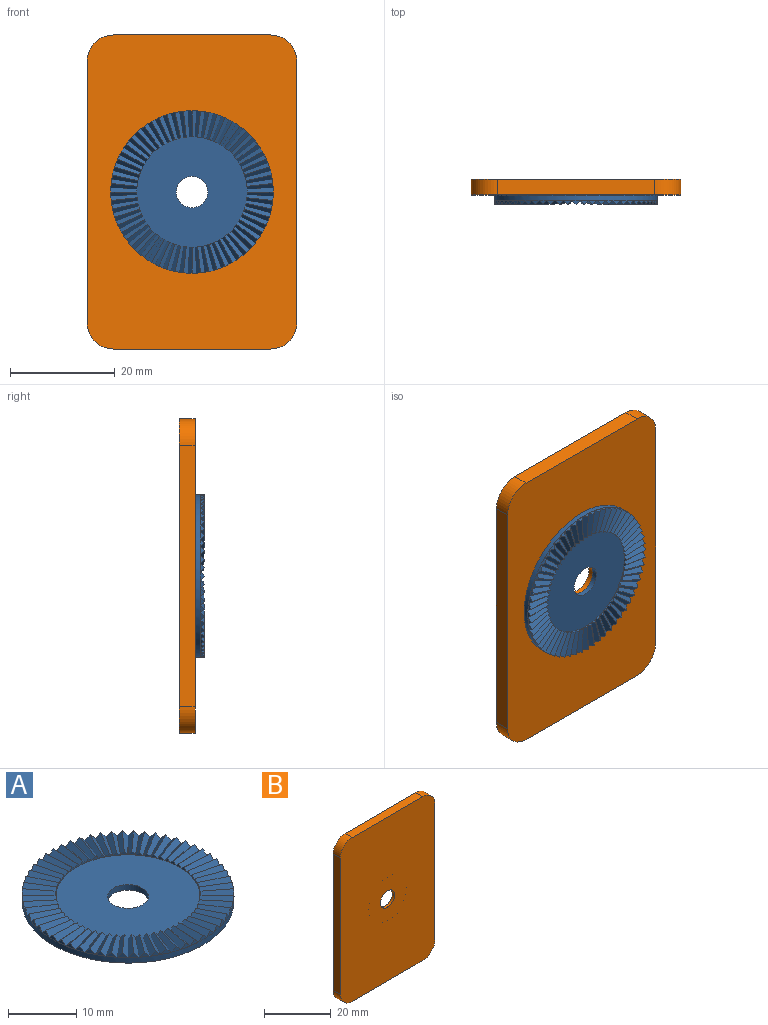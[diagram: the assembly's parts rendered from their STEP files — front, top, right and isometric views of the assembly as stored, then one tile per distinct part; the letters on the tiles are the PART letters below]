
ASSEMBLY  parts=2 mates=1
PART A: 364 faces, bbox 31x31x1.8 mm
  f0: plane 30.96x30.96mm, normal (0,0,1), area 322.4mm2, adj f1,f2,f6,f7,f9,f12,f13,f15
  f1: cylinder r=3mm len=6mm, axis (0,0,1), area 18.8mm2, adj f0,f3
  f2: cylinder r=15.5mm len=31mm, axis (0,0,1), area 97.4mm2, adj f0,f3,f4,f8,f10,f14,f16,f20
  f3: plane 31x31mm, normal (0,0,-1), area 726.5mm2, adj f1,f2
  f4: plane 0.81x0.02mm, normal (0,0,-1), area 0mm2, adj f2,f5,f9
  f5: plane 1.62x0.81mm, normal (-1,0,0), area 0.7mm2, adj f4,f7,f8,f9
  f6: plane 1.1x0.55mm, normal (1,0,0), area 0.3mm2, adj f0,f7,f9
  f7: plane 4.95x0.81mm, normal (0.04,-0.71,0.71), area 4.8mm2, adj f0,f5,f6,f8,f9
  f8: plane 0.81x0.02mm, normal (0,0,-1), area 0mm2, adj f2,f5,f7
  f9: plane 4.95x0.81mm, normal (0.04,0.71,0.71), area 4.8mm2, adj f0,f4,f5,f6,f7
  f10: plane 0.81x0.08mm, normal (0,0,-1), area 0mm2, adj f2,f11,f15
  f11: plane 1.61x0.81mm, normal (-0.99,-0.1,0), area 0.7mm2, adj f10,f13,f14,f15
  f12: plane 1.1x0.55mm, normal (0.99,0.1,0), area 0.3mm2, adj f0,f13,f15
  f13: plane 4.98x1.32mm, normal (0.11,-0.7,0.71), area 4.8mm2, adj f0,f11,f12,f14,f15
  f14: plane 0.81x0.11mm, normal (0,0,-1), area 0mm2, adj f2,f11,f13
  f15: plane 5.01x1.07mm, normal (-0.04,0.71,0.71), area 4.8mm2, adj f0,f10,f11,f12,f13
  f16: plane 0.8x0.17mm, normal (0,0,-1), area 0mm2, adj f2,f17,f21
  f17: plane 1.59x0.81mm, normal (-0.98,-0.21,0), area 0.7mm2, adj f16,f19,f20,f21
  f18: plane 1.08x0.55mm, normal (0.98,0.21,0), area 0.3mm2, adj f0,f19,f21
  f19: plane 4.95x1.82mm, normal (0.18,-0.68,0.71), area 4.8mm2, adj f0,f17,f18,f20,f21
  f20: plane 0.79x0.19mm, normal (0,0,-1), area 0mm2, adj f2,f17,f19
  f21: plane 5.01x1.57mm, normal (-0.11,0.7,0.71), area 4.8mm2, adj f0,f16,f17,f18,f19
  f22: plane 0.78x0.25mm, normal (0,0,-1), area 0mm2, adj f2,f23,f27
  f23: plane 1.54x0.81mm, normal (-0.95,-0.31,0), area 0.7mm2, adj f22,f25,f26,f27
  f24: plane 1.05x0.55mm, normal (0.95,0.31,0), area 0.3mm2, adj f0,f25,f27
  f25: plane 4.88x2.3mm, normal (0.25,-0.66,0.71), area 4.8mm2, adj f0,f23,f24,f26,f27
  f26: plane 0.77x0.27mm, normal (0,0,-1), area 0mm2, adj f2,f23,f25
  f27: plane 4.96x2.05mm, normal (-0.18,0.68,0.71), area 4.8mm2, adj f0,f22,f23,f24,f25
  f28: plane 0.75x0.33mm, normal (0,0,-1), area 0mm2, adj f2,f29,f33
  f29: plane 1.48x0.81mm, normal (-0.91,-0.41,0), area 0.7mm2, adj f28,f31,f32,f33
  f30: plane 1.01x0.55mm, normal (0.91,0.41,0), area 0.3mm2, adj f0,f31,f33
  f31: plane 4.74x2.75mm, normal (0.32,-0.63,0.71), area 4.8mm2, adj f0,f29,f30,f32,f33
  f32: plane 0.74x0.35mm, normal (0,0,-1), area 0mm2, adj f2,f29,f31
  f33: plane 4.85x2.52mm, normal (-0.25,0.66,0.71), area 4.8mm2, adj f0,f28,f29,f30,f31
  f34: plane 0.71x0.41mm, normal (0,0,-1), area 0mm2, adj f2,f35,f39
  f35: plane 1.41x0.81mm, normal (-0.87,-0.5,0), area 0.7mm2, adj f34,f37,f38,f39
  f36: plane 0.96x0.55mm, normal (0.87,0.5,0), area 0.3mm2, adj f0,f37,f39
  f37: plane 4.56x3.18mm, normal (0.39,-0.59,0.71), area 4.8mm2, adj f0,f35,f36,f38,f39
  f38: plane 0.7x0.42mm, normal (0,0,-1), area 0mm2, adj f2,f35,f37
  f39: plane 4.69x2.95mm, normal (-0.32,0.63,0.71), area 4.8mm2, adj f0,f34,f35,f36,f37
  f40: plane 0.67x0.48mm, normal (0,0,-1), area 0mm2, adj f2,f41,f45
  f41: plane 1.31x0.95mm, normal (-0.81,-0.59,0), area 0.7mm2, adj f40,f43,f44,f45
  f42: plane 0.89x0.65mm, normal (0.81,0.59,0), area 0.3mm2, adj f0,f43,f45
  f43: plane 4.33x3.56mm, normal (0.45,-0.55,0.71), area 4.8mm2, adj f0,f41,f42,f44,f45
  f44: plane 0.66x0.49mm, normal (0,0,-1), area 0mm2, adj f2,f41,f43
  f45: plane 4.48x3.36mm, normal (-0.39,0.59,0.71), area 4.8mm2, adj f0,f40,f41,f42,f43
  f46: plane 0.62x0.54mm, normal (0,0,-1), area 0mm2, adj f2,f47,f51
  f47: plane 1.21x1.09mm, normal (-0.74,-0.67,0), area 0.7mm2, adj f46,f49,f50,f51
  f48: plane 0.82x0.74mm, normal (0.74,0.67,0), area 0.3mm2, adj f0,f49,f51
  f49: plane 4.05x3.91mm, normal (0.5,-0.5,0.71), area 4.8mm2, adj f0,f47,f48,f50,f51
  f50: plane 0.6x0.56mm, normal (0,0,-1), area 0mm2, adj f2,f47,f49
  f51: plane 4.22x3.72mm, normal (-0.45,0.55,0.71), area 4.8mm2, adj f0,f46,f47,f48,f49
  f52: plane 0.6x0.56mm, normal (0,0,-1), area 0mm2, adj f2,f53,f57
  f53: plane 1.21x1.09mm, normal (-0.67,-0.74,0), area 0.7mm2, adj f52,f55,f56,f57
  f54: plane 0.82x0.74mm, normal (0.67,0.74,0), area 0.3mm2, adj f0,f55,f57
  f55: plane 4.22x3.72mm, normal (0.55,-0.45,0.71), area 4.8mm2, adj f0,f53,f54,f56,f57
  f56: plane 0.62x0.54mm, normal (0,0,-1), area 0mm2, adj f2,f53,f55
  f57: plane 4.05x3.91mm, normal (-0.5,0.5,0.71), area 4.8mm2, adj f0,f52,f53,f54,f55
  f58: plane 0.66x0.49mm, normal (0,0,-1), area 0mm2, adj f2,f59,f63
  f59: plane 1.31x0.95mm, normal (-0.59,-0.81,0), area 0.7mm2, adj f58,f61,f62,f63
  f60: plane 0.89x0.65mm, normal (0.59,0.81,0), area 0.3mm2, adj f0,f61,f63
  f61: plane 4.48x3.36mm, normal (0.59,-0.39,0.71), area 4.8mm2, adj f0,f59,f60,f62,f63
  f62: plane 0.67x0.48mm, normal (0,0,-1), area 0mm2, adj f2,f59,f61
  f63: plane 4.33x3.56mm, normal (-0.55,0.45,0.71), area 4.8mm2, adj f0,f58,f59,f60,f61
  f64: plane 0.7x0.42mm, normal (0,0,-1), area 0mm2, adj f2,f65,f69
  f65: plane 1.41x0.81mm, normal (-0.5,-0.87,0), area 0.7mm2, adj f64,f67,f68,f69
  f66: plane 0.96x0.55mm, normal (0.5,0.87,0), area 0.3mm2, adj f0,f67,f69
  f67: plane 4.69x2.95mm, normal (0.63,-0.32,0.71), area 4.8mm2, adj f0,f65,f66,f68,f69
  f68: plane 0.71x0.41mm, normal (0,0,-1), area 0mm2, adj f2,f65,f67
  f69: plane 4.56x3.18mm, normal (-0.59,0.39,0.71), area 4.8mm2, adj f0,f64,f65,f66,f67
  f70: plane 0.74x0.35mm, normal (0,0,-1), area 0mm2, adj f2,f71,f75
  f71: plane 1.48x0.81mm, normal (-0.41,-0.91,0), area 0.7mm2, adj f70,f73,f74,f75
  f72: plane 1.01x0.55mm, normal (0.41,0.91,0), area 0.3mm2, adj f0,f73,f75
  f73: plane 4.85x2.52mm, normal (0.66,-0.25,0.71), area 4.8mm2, adj f0,f71,f72,f74,f75
  f74: plane 0.75x0.33mm, normal (0,0,-1), area 0mm2, adj f2,f71,f73
  f75: plane 4.74x2.75mm, normal (-0.63,0.32,0.71), area 4.8mm2, adj f0,f70,f71,f72,f73
  f76: plane 0.77x0.27mm, normal (0,0,-1), area 0mm2, adj f2,f77,f81
  f77: plane 1.54x0.81mm, normal (-0.31,-0.95,0), area 0.7mm2, adj f76,f79,f80,f81
  f78: plane 1.05x0.55mm, normal (0.31,0.95,0), area 0.3mm2, adj f0,f79,f81
  f79: plane 4.96x2.05mm, normal (0.68,-0.18,0.71), area 4.8mm2, adj f0,f77,f78,f80,f81
  f80: plane 0.78x0.25mm, normal (0,0,-1), area 0mm2, adj f2,f77,f79
  f81: plane 4.88x2.3mm, normal (-0.66,0.25,0.71), area 4.8mm2, adj f0,f76,f77,f78,f79
  f82: plane 0.79x0.19mm, normal (0,0,-1), area 0mm2, adj f2,f83,f87
  f83: plane 1.59x0.81mm, normal (-0.21,-0.98,0), area 0.7mm2, adj f82,f85,f86,f87
  f84: plane 1.08x0.55mm, normal (0.21,0.98,0), area 0.3mm2, adj f0,f85,f87
  f85: plane 5.01x1.57mm, normal (0.7,-0.11,0.71), area 4.8mm2, adj f0,f83,f84,f86,f87
  f86: plane 0.8x0.17mm, normal (0,0,-1), area 0mm2, adj f2,f83,f85
  f87: plane 4.95x1.82mm, normal (-0.68,0.18,0.71), area 4.8mm2, adj f0,f82,f83,f84,f85
  f88: plane 0.81x0.11mm, normal (0,0,-1), area 0mm2, adj f2,f89,f93
  f89: plane 1.61x0.81mm, normal (-0.1,-0.99,0), area 0.7mm2, adj f88,f91,f92,f93
  f90: plane 1.1x0.55mm, normal (0.1,0.99,0), area 0.3mm2, adj f0,f91,f93
  f91: plane 5.01x1.07mm, normal (0.71,-0.04,0.71), area 4.8mm2, adj f0,f89,f90,f92,f93
  f92: plane 0.81x0.08mm, normal (0,0,-1), area 0mm2, adj f2,f89,f91
  f93: plane 4.98x1.32mm, normal (-0.7,0.11,0.71), area 4.8mm2, adj f0,f88,f89,f90,f91
  f94: plane 0.81x0.02mm, normal (0,0,-1), area 0mm2, adj f2,f95,f99
  f95: plane 1.62x0.81mm, normal (0,-1,0), area 0.7mm2, adj f94,f97,f98,f99
  f96: plane 1.1x0.55mm, normal (0,1,0), area 0.3mm2, adj f0,f97,f99
  f97: plane 4.95x0.81mm, normal (0.71,0.04,0.71), area 4.8mm2, adj f0,f95,f96,f98,f99
  f98: plane 0.81x0.02mm, normal (0,0,-1), area 0mm2, adj f2,f95,f97
  f99: plane 4.95x0.81mm, normal (-0.71,0.04,0.71), area 4.8mm2, adj f0,f94,f95,f96,f97
  f100: plane 0.81x0.08mm, normal (0,0,-1), area 0mm2, adj f2,f101,f105
  f101: plane 1.61x0.81mm, normal (0.1,-0.99,0), area 0.7mm2, adj f100,f103,f104,f105
  f102: plane 1.1x0.55mm, normal (-0.1,0.99,0), area 0.3mm2, adj f0,f103,f105
  f103: plane 4.98x1.32mm, normal (0.7,0.11,0.71), area 4.8mm2, adj f0,f101,f102,f104,f105
  f104: plane 0.81x0.11mm, normal (0,0,-1), area 0mm2, adj f2,f101,f103
  f105: plane 5.01x1.07mm, normal (-0.71,-0.04,0.71), area 4.8mm2, adj f0,f100,f101,f102,f103
  f106: plane 0.8x0.17mm, normal (0,0,-1), area 0mm2, adj f2,f107,f111
  f107: plane 1.59x0.81mm, normal (0.21,-0.98,0), area 0.7mm2, adj f106,f109,f110,f111
  f108: plane 1.08x0.55mm, normal (-0.21,0.98,0), area 0.3mm2, adj f0,f109,f111
  f109: plane 4.95x1.82mm, normal (0.68,0.18,0.71), area 4.8mm2, adj f0,f107,f108,f110,f111
  f110: plane 0.79x0.19mm, normal (0,0,-1), area 0mm2, adj f2,f107,f109
  f111: plane 5.01x1.57mm, normal (-0.7,-0.11,0.71), area 4.8mm2, adj f0,f106,f107,f108,f109
  f112: plane 0.78x0.25mm, normal (0,0,-1), area 0mm2, adj f2,f113,f117
  f113: plane 1.54x0.81mm, normal (0.31,-0.95,0), area 0.7mm2, adj f112,f115,f116,f117
  f114: plane 1.05x0.55mm, normal (-0.31,0.95,0), area 0.3mm2, adj f0,f115,f117
  f115: plane 4.88x2.3mm, normal (0.66,0.25,0.71), area 4.8mm2, adj f0,f113,f114,f116,f117
  f116: plane 0.77x0.27mm, normal (0,0,-1), area 0mm2, adj f2,f113,f115
  f117: plane 4.96x2.05mm, normal (-0.68,-0.18,0.71), area 4.8mm2, adj f0,f112,f113,f114,f115
  f118: plane 0.75x0.33mm, normal (0,0,-1), area 0mm2, adj f2,f119,f123
  f119: plane 1.48x0.81mm, normal (0.41,-0.91,0), area 0.7mm2, adj f118,f121,f122,f123
  f120: plane 1.01x0.55mm, normal (-0.41,0.91,0), area 0.3mm2, adj f0,f121,f123
  f121: plane 4.74x2.75mm, normal (0.63,0.32,0.71), area 4.8mm2, adj f0,f119,f120,f122,f123
  f122: plane 0.74x0.35mm, normal (0,0,-1), area 0mm2, adj f2,f119,f121
  f123: plane 4.85x2.52mm, normal (-0.66,-0.25,0.71), area 4.8mm2, adj f0,f118,f119,f120,f121
  f124: plane 0.71x0.41mm, normal (0,0,-1), area 0mm2, adj f2,f125,f129
  f125: plane 1.41x0.81mm, normal (0.5,-0.87,0), area 0.7mm2, adj f124,f127,f128,f129
  f126: plane 0.96x0.55mm, normal (-0.5,0.87,0), area 0.3mm2, adj f0,f127,f129
  f127: plane 4.56x3.18mm, normal (0.59,0.39,0.71), area 4.8mm2, adj f0,f125,f126,f128,f129
  f128: plane 0.7x0.42mm, normal (0,0,-1), area 0mm2, adj f2,f125,f127
  f129: plane 4.69x2.95mm, normal (-0.63,-0.32,0.71), area 4.8mm2, adj f0,f124,f125,f126,f127
  f130: plane 0.67x0.48mm, normal (0,0,-1), area 0mm2, adj f2,f131,f135
  f131: plane 1.31x0.95mm, normal (0.59,-0.81,0), area 0.7mm2, adj f130,f133,f134,f135
  f132: plane 0.89x0.65mm, normal (-0.59,0.81,0), area 0.3mm2, adj f0,f133,f135
  f133: plane 4.33x3.56mm, normal (0.55,0.45,0.71), area 4.8mm2, adj f0,f131,f132,f134,f135
  f134: plane 0.66x0.49mm, normal (0,0,-1), area 0mm2, adj f2,f131,f133
  f135: plane 4.48x3.36mm, normal (-0.59,-0.39,0.71), area 4.8mm2, adj f0,f130,f131,f132,f133
  f136: plane 0.62x0.54mm, normal (0,0,-1), area 0mm2, adj f2,f137,f141
  f137: plane 1.21x1.09mm, normal (0.67,-0.74,0), area 0.7mm2, adj f136,f139,f140,f141
  f138: plane 0.82x0.74mm, normal (-0.67,0.74,0), area 0.3mm2, adj f0,f139,f141
  f139: plane 4.05x3.91mm, normal (0.5,0.5,0.71), area 4.8mm2, adj f0,f137,f138,f140,f141
  f140: plane 0.6x0.56mm, normal (0,0,-1), area 0mm2, adj f2,f137,f139
  f141: plane 4.22x3.72mm, normal (-0.55,-0.45,0.71), area 4.8mm2, adj f0,f136,f137,f138,f139
  f142: plane 0.6x0.56mm, normal (0,0,-1), area 0mm2, adj f2,f143,f147
  f143: plane 1.21x1.09mm, normal (0.74,-0.67,0), area 0.7mm2, adj f142,f145,f146,f147
  f144: plane 0.82x0.74mm, normal (-0.74,0.67,0), area 0.3mm2, adj f0,f145,f147
  f145: plane 4.22x3.72mm, normal (0.45,0.55,0.71), area 4.8mm2, adj f0,f143,f144,f146,f147
  f146: plane 0.62x0.54mm, normal (0,0,-1), area 0mm2, adj f2,f143,f145
  f147: plane 4.05x3.91mm, normal (-0.5,-0.5,0.71), area 4.8mm2, adj f0,f142,f143,f144,f145
  f148: plane 0.66x0.49mm, normal (0,0,-1), area 0mm2, adj f2,f149,f153
  f149: plane 1.31x0.95mm, normal (0.81,-0.59,0), area 0.7mm2, adj f148,f151,f152,f153
  f150: plane 0.89x0.65mm, normal (-0.81,0.59,0), area 0.3mm2, adj f0,f151,f153
  f151: plane 4.48x3.36mm, normal (0.39,0.59,0.71), area 4.8mm2, adj f0,f149,f150,f152,f153
  f152: plane 0.67x0.48mm, normal (0,0,-1), area 0mm2, adj f2,f149,f151
  f153: plane 4.33x3.56mm, normal (-0.45,-0.55,0.71), area 4.8mm2, adj f0,f148,f149,f150,f151
  f154: plane 0.7x0.42mm, normal (0,0,-1), area 0mm2, adj f2,f155,f159
  f155: plane 1.41x0.81mm, normal (0.87,-0.5,0), area 0.7mm2, adj f154,f157,f158,f159
  f156: plane 0.96x0.55mm, normal (-0.87,0.5,0), area 0.3mm2, adj f0,f157,f159
  f157: plane 4.69x2.95mm, normal (0.32,0.63,0.71), area 4.8mm2, adj f0,f155,f156,f158,f159
  f158: plane 0.71x0.41mm, normal (0,0,-1), area 0mm2, adj f2,f155,f157
  f159: plane 4.56x3.18mm, normal (-0.39,-0.59,0.71), area 4.8mm2, adj f0,f154,f155,f156,f157
  f160: plane 0.74x0.35mm, normal (0,0,-1), area 0mm2, adj f2,f161,f165
  f161: plane 1.48x0.81mm, normal (0.91,-0.41,0), area 0.7mm2, adj f160,f163,f164,f165
  f162: plane 1.01x0.55mm, normal (-0.91,0.41,0), area 0.3mm2, adj f0,f163,f165
  f163: plane 4.85x2.52mm, normal (0.25,0.66,0.71), area 4.8mm2, adj f0,f161,f162,f164,f165
  f164: plane 0.75x0.33mm, normal (0,0,-1), area 0mm2, adj f2,f161,f163
  f165: plane 4.74x2.75mm, normal (-0.32,-0.63,0.71), area 4.8mm2, adj f0,f160,f161,f162,f163
  f166: plane 0.77x0.27mm, normal (0,0,-1), area 0mm2, adj f2,f167,f171
  f167: plane 1.54x0.81mm, normal (0.95,-0.31,0), area 0.7mm2, adj f166,f169,f170,f171
  f168: plane 1.05x0.55mm, normal (-0.95,0.31,0), area 0.3mm2, adj f0,f169,f171
  f169: plane 4.96x2.05mm, normal (0.18,0.68,0.71), area 4.8mm2, adj f0,f167,f168,f170,f171
  f170: plane 0.78x0.25mm, normal (0,0,-1), area 0mm2, adj f2,f167,f169
  f171: plane 4.88x2.3mm, normal (-0.25,-0.66,0.71), area 4.8mm2, adj f0,f166,f167,f168,f169
  f172: plane 0.79x0.19mm, normal (0,0,-1), area 0mm2, adj f2,f173,f177
  f173: plane 1.59x0.81mm, normal (0.98,-0.21,0), area 0.7mm2, adj f172,f175,f176,f177
  f174: plane 1.08x0.55mm, normal (-0.98,0.21,0), area 0.3mm2, adj f0,f175,f177
  f175: plane 5.01x1.57mm, normal (0.11,0.7,0.71), area 4.8mm2, adj f0,f173,f174,f176,f177
  f176: plane 0.8x0.17mm, normal (0,0,-1), area 0mm2, adj f2,f173,f175
  f177: plane 4.95x1.82mm, normal (-0.18,-0.68,0.71), area 4.8mm2, adj f0,f172,f173,f174,f175
  f178: plane 0.81x0.11mm, normal (0,0,-1), area 0mm2, adj f2,f179,f183
  f179: plane 1.61x0.81mm, normal (0.99,-0.1,0), area 0.7mm2, adj f178,f181,f182,f183
  f180: plane 1.1x0.55mm, normal (-0.99,0.1,0), area 0.3mm2, adj f0,f181,f183
  f181: plane 5.01x1.07mm, normal (0.04,0.71,0.71), area 4.8mm2, adj f0,f179,f180,f182,f183
  f182: plane 0.81x0.08mm, normal (0,0,-1), area 0mm2, adj f2,f179,f181
  f183: plane 4.98x1.32mm, normal (-0.11,-0.7,0.71), area 4.8mm2, adj f0,f178,f179,f180,f181
  f184: plane 0.81x0.02mm, normal (0,0,-1), area 0mm2, adj f2,f185,f189
  f185: plane 1.62x0.81mm, normal (1,0,0), area 0.7mm2, adj f184,f187,f188,f189
  f186: plane 1.1x0.55mm, normal (-1,0,0), area 0.3mm2, adj f0,f187,f189
  f187: plane 4.95x0.81mm, normal (-0.04,0.71,0.71), area 4.8mm2, adj f0,f185,f186,f188,f189
  f188: plane 0.81x0.02mm, normal (0,0,-1), area 0mm2, adj f2,f185,f187
  f189: plane 4.95x0.81mm, normal (-0.04,-0.71,0.71), area 4.8mm2, adj f0,f184,f185,f186,f187
  f190: plane 0.81x0.08mm, normal (0,0,-1), area 0mm2, adj f2,f191,f195
  f191: plane 1.61x0.81mm, normal (0.99,0.1,0), area 0.7mm2, adj f190,f193,f194,f195
  f192: plane 1.1x0.55mm, normal (-0.99,-0.1,0), area 0.3mm2, adj f0,f193,f195
  f193: plane 4.98x1.32mm, normal (-0.11,0.7,0.71), area 4.8mm2, adj f0,f191,f192,f194,f195
  f194: plane 0.81x0.11mm, normal (0,0,-1), area 0mm2, adj f2,f191,f193
  f195: plane 5.01x1.07mm, normal (0.04,-0.71,0.71), area 4.8mm2, adj f0,f190,f191,f192,f193
  f196: plane 0.8x0.17mm, normal (0,0,-1), area 0mm2, adj f2,f197,f201
  f197: plane 1.59x0.81mm, normal (0.98,0.21,0), area 0.7mm2, adj f196,f199,f200,f201
  f198: plane 1.08x0.55mm, normal (-0.98,-0.21,0), area 0.3mm2, adj f0,f199,f201
  f199: plane 4.95x1.82mm, normal (-0.18,0.68,0.71), area 4.8mm2, adj f0,f197,f198,f200,f201
  f200: plane 0.79x0.19mm, normal (0,0,-1), area 0mm2, adj f2,f197,f199
  f201: plane 5.01x1.57mm, normal (0.11,-0.7,0.71), area 4.8mm2, adj f0,f196,f197,f198,f199
  f202: plane 0.78x0.25mm, normal (0,0,-1), area 0mm2, adj f2,f203,f207
  f203: plane 1.54x0.81mm, normal (0.95,0.31,0), area 0.7mm2, adj f202,f205,f206,f207
  f204: plane 1.05x0.55mm, normal (-0.95,-0.31,0), area 0.3mm2, adj f0,f205,f207
  f205: plane 4.88x2.3mm, normal (-0.25,0.66,0.71), area 4.8mm2, adj f0,f203,f204,f206,f207
  f206: plane 0.77x0.27mm, normal (0,0,-1), area 0mm2, adj f2,f203,f205
  f207: plane 4.96x2.05mm, normal (0.18,-0.68,0.71), area 4.8mm2, adj f0,f202,f203,f204,f205
  f208: plane 0.75x0.33mm, normal (0,0,-1), area 0mm2, adj f2,f209,f213
  f209: plane 1.48x0.81mm, normal (0.91,0.41,0), area 0.7mm2, adj f208,f211,f212,f213
  f210: plane 1.01x0.55mm, normal (-0.91,-0.41,0), area 0.3mm2, adj f0,f211,f213
  f211: plane 4.74x2.75mm, normal (-0.32,0.63,0.71), area 4.8mm2, adj f0,f209,f210,f212,f213
  f212: plane 0.74x0.35mm, normal (0,0,-1), area 0mm2, adj f2,f209,f211
  f213: plane 4.85x2.52mm, normal (0.25,-0.66,0.71), area 4.8mm2, adj f0,f208,f209,f210,f211
  f214: plane 0.71x0.41mm, normal (0,0,-1), area 0mm2, adj f2,f215,f219
  f215: plane 1.41x0.81mm, normal (0.87,0.5,0), area 0.7mm2, adj f214,f217,f218,f219
  f216: plane 0.96x0.55mm, normal (-0.87,-0.5,0), area 0.3mm2, adj f0,f217,f219
  f217: plane 4.56x3.18mm, normal (-0.39,0.59,0.71), area 4.8mm2, adj f0,f215,f216,f218,f219
  f218: plane 0.7x0.42mm, normal (0,0,-1), area 0mm2, adj f2,f215,f217
  f219: plane 4.69x2.95mm, normal (0.32,-0.63,0.71), area 4.8mm2, adj f0,f214,f215,f216,f217
  f220: plane 0.67x0.48mm, normal (0,0,-1), area 0mm2, adj f2,f221,f225
  f221: plane 1.31x0.95mm, normal (0.81,0.59,0), area 0.7mm2, adj f220,f223,f224,f225
  f222: plane 0.89x0.65mm, normal (-0.81,-0.59,0), area 0.3mm2, adj f0,f223,f225
  f223: plane 4.33x3.56mm, normal (-0.45,0.55,0.71), area 4.8mm2, adj f0,f221,f222,f224,f225
  f224: plane 0.66x0.49mm, normal (0,0,-1), area 0mm2, adj f2,f221,f223
  f225: plane 4.48x3.36mm, normal (0.39,-0.59,0.71), area 4.8mm2, adj f0,f220,f221,f222,f223
  f226: plane 0.62x0.54mm, normal (0,0,-1), area 0mm2, adj f2,f227,f231
  f227: plane 1.21x1.09mm, normal (0.74,0.67,0), area 0.7mm2, adj f226,f229,f230,f231
  f228: plane 0.82x0.74mm, normal (-0.74,-0.67,0), area 0.3mm2, adj f0,f229,f231
  f229: plane 4.05x3.91mm, normal (-0.5,0.5,0.71), area 4.8mm2, adj f0,f227,f228,f230,f231
  f230: plane 0.6x0.56mm, normal (0,0,-1), area 0mm2, adj f2,f227,f229
  f231: plane 4.22x3.72mm, normal (0.45,-0.55,0.71), area 4.8mm2, adj f0,f226,f227,f228,f229
  f232: plane 0.6x0.56mm, normal (0,0,-1), area 0mm2, adj f2,f233,f237
  f233: plane 1.21x1.09mm, normal (0.67,0.74,0), area 0.7mm2, adj f232,f235,f236,f237
  f234: plane 0.82x0.74mm, normal (-0.67,-0.74,0), area 0.3mm2, adj f0,f235,f237
  f235: plane 4.22x3.72mm, normal (-0.55,0.45,0.71), area 4.8mm2, adj f0,f233,f234,f236,f237
  f236: plane 0.62x0.54mm, normal (0,0,-1), area 0mm2, adj f2,f233,f235
  f237: plane 4.05x3.91mm, normal (0.5,-0.5,0.71), area 4.8mm2, adj f0,f232,f233,f234,f235
  f238: plane 0.66x0.49mm, normal (0,0,-1), area 0mm2, adj f2,f239,f243
  f239: plane 1.31x0.95mm, normal (0.59,0.81,0), area 0.7mm2, adj f238,f241,f242,f243
  f240: plane 0.89x0.65mm, normal (-0.59,-0.81,0), area 0.3mm2, adj f0,f241,f243
  f241: plane 4.48x3.36mm, normal (-0.59,0.39,0.71), area 4.8mm2, adj f0,f239,f240,f242,f243
  f242: plane 0.67x0.48mm, normal (0,0,-1), area 0mm2, adj f2,f239,f241
  f243: plane 4.33x3.56mm, normal (0.55,-0.45,0.71), area 4.8mm2, adj f0,f238,f239,f240,f241
  f244: plane 0.7x0.42mm, normal (0,0,-1), area 0mm2, adj f2,f245,f249
  f245: plane 1.41x0.81mm, normal (0.5,0.87,0), area 0.7mm2, adj f244,f247,f248,f249
  f246: plane 0.96x0.55mm, normal (-0.5,-0.87,0), area 0.3mm2, adj f0,f247,f249
  f247: plane 4.69x2.95mm, normal (-0.63,0.32,0.71), area 4.8mm2, adj f0,f245,f246,f248,f249
  f248: plane 0.71x0.41mm, normal (0,0,-1), area 0mm2, adj f2,f245,f247
  f249: plane 4.56x3.18mm, normal (0.59,-0.39,0.71), area 4.8mm2, adj f0,f244,f245,f246,f247
  f250: plane 0.74x0.35mm, normal (0,0,-1), area 0mm2, adj f2,f251,f255
  f251: plane 1.48x0.81mm, normal (0.41,0.91,0), area 0.7mm2, adj f250,f253,f254,f255
  f252: plane 1.01x0.55mm, normal (-0.41,-0.91,0), area 0.3mm2, adj f0,f253,f255
  f253: plane 4.85x2.52mm, normal (-0.66,0.25,0.71), area 4.8mm2, adj f0,f251,f252,f254,f255
  f254: plane 0.75x0.33mm, normal (0,0,-1), area 0mm2, adj f2,f251,f253
  f255: plane 4.74x2.75mm, normal (0.63,-0.32,0.71), area 4.8mm2, adj f0,f250,f251,f252,f253
  f256: plane 0.77x0.27mm, normal (0,0,-1), area 0mm2, adj f2,f257,f261
  f257: plane 1.54x0.81mm, normal (0.31,0.95,0), area 0.7mm2, adj f256,f259,f260,f261
  f258: plane 1.05x0.55mm, normal (-0.31,-0.95,0), area 0.3mm2, adj f0,f259,f261
  f259: plane 4.96x2.05mm, normal (-0.68,0.18,0.71), area 4.8mm2, adj f0,f257,f258,f260,f261
  f260: plane 0.78x0.25mm, normal (0,0,-1), area 0mm2, adj f2,f257,f259
  f261: plane 4.88x2.3mm, normal (0.66,-0.25,0.71), area 4.8mm2, adj f0,f256,f257,f258,f259
  f262: plane 0.79x0.19mm, normal (0,0,-1), area 0mm2, adj f2,f263,f267
  f263: plane 1.59x0.81mm, normal (0.21,0.98,0), area 0.7mm2, adj f262,f265,f266,f267
  f264: plane 1.08x0.55mm, normal (-0.21,-0.98,0), area 0.3mm2, adj f0,f265,f267
  f265: plane 5.01x1.57mm, normal (-0.7,0.11,0.71), area 4.8mm2, adj f0,f263,f264,f266,f267
  f266: plane 0.8x0.17mm, normal (0,0,-1), area 0mm2, adj f2,f263,f265
  f267: plane 4.95x1.82mm, normal (0.68,-0.18,0.71), area 4.8mm2, adj f0,f262,f263,f264,f265
  f268: plane 0.81x0.11mm, normal (0,0,-1), area 0mm2, adj f2,f269,f273
  f269: plane 1.61x0.81mm, normal (0.1,0.99,0), area 0.7mm2, adj f268,f271,f272,f273
  f270: plane 1.1x0.55mm, normal (-0.1,-0.99,0), area 0.3mm2, adj f0,f271,f273
  f271: plane 5.01x1.07mm, normal (-0.71,0.04,0.71), area 4.8mm2, adj f0,f269,f270,f272,f273
  f272: plane 0.81x0.08mm, normal (0,0,-1), area 0mm2, adj f2,f269,f271
  f273: plane 4.98x1.32mm, normal (0.7,-0.11,0.71), area 4.8mm2, adj f0,f268,f269,f270,f271
  f274: plane 0.81x0.02mm, normal (0,0,-1), area 0mm2, adj f2,f275,f277
  f275: plane 1.62x0.81mm, normal (0,1,0), area 0.7mm2, adj f274,f277,f278,f279
  f276: plane 1.1x0.55mm, normal (0,-1,0), area 0.3mm2, adj f0,f277,f279
  f277: plane 4.95x0.81mm, normal (-0.71,-0.04,0.71), area 4.8mm2, adj f0,f274,f275,f276,f279
  f278: plane 0.81x0.02mm, normal (0,0,-1), area 0mm2, adj f2,f275,f279
  f279: plane 4.95x0.81mm, normal (0.71,-0.04,0.71), area 4.8mm2, adj f0,f275,f276,f277,f278
  f280: plane 0.81x0.08mm, normal (0,0,-1), area 0mm2, adj f2,f281,f285
  f281: plane 1.61x0.81mm, normal (-0.1,0.99,0), area 0.7mm2, adj f280,f283,f284,f285
  f282: plane 1.1x0.55mm, normal (0.1,-0.99,0), area 0.3mm2, adj f0,f283,f285
  f283: plane 4.98x1.32mm, normal (-0.7,-0.11,0.71), area 4.8mm2, adj f0,f281,f282,f284,f285
  f284: plane 0.81x0.11mm, normal (0,0,-1), area 0mm2, adj f2,f281,f283
  f285: plane 5.01x1.07mm, normal (0.71,0.04,0.71), area 4.8mm2, adj f0,f280,f281,f282,f283
  f286: plane 0.8x0.17mm, normal (0,0,-1), area 0mm2, adj f2,f287,f291
  f287: plane 1.59x0.81mm, normal (-0.21,0.98,0), area 0.7mm2, adj f286,f289,f290,f291
  f288: plane 1.08x0.55mm, normal (0.21,-0.98,0), area 0.3mm2, adj f0,f289,f291
  f289: plane 4.95x1.82mm, normal (-0.68,-0.18,0.71), area 4.8mm2, adj f0,f287,f288,f290,f291
  f290: plane 0.79x0.19mm, normal (0,0,-1), area 0mm2, adj f2,f287,f289
  f291: plane 5.01x1.57mm, normal (0.7,0.11,0.71), area 4.8mm2, adj f0,f286,f287,f288,f289
  f292: plane 0.78x0.25mm, normal (0,0,-1), area 0mm2, adj f2,f293,f297
  f293: plane 1.54x0.81mm, normal (-0.31,0.95,0), area 0.7mm2, adj f292,f295,f296,f297
  f294: plane 1.05x0.55mm, normal (0.31,-0.95,0), area 0.3mm2, adj f0,f295,f297
  f295: plane 4.88x2.3mm, normal (-0.66,-0.25,0.71), area 4.8mm2, adj f0,f293,f294,f296,f297
  f296: plane 0.77x0.27mm, normal (0,0,-1), area 0mm2, adj f2,f293,f295
  f297: plane 4.96x2.05mm, normal (0.68,0.18,0.71), area 4.8mm2, adj f0,f292,f293,f294,f295
  f298: plane 0.75x0.33mm, normal (0,0,-1), area 0mm2, adj f2,f299,f303
  f299: plane 1.48x0.81mm, normal (-0.41,0.91,0), area 0.7mm2, adj f298,f301,f302,f303
  f300: plane 1.01x0.55mm, normal (0.41,-0.91,0), area 0.3mm2, adj f0,f301,f303
  f301: plane 4.74x2.75mm, normal (-0.63,-0.32,0.71), area 4.8mm2, adj f0,f299,f300,f302,f303
  f302: plane 0.74x0.35mm, normal (0,0,-1), area 0mm2, adj f2,f299,f301
  f303: plane 4.85x2.52mm, normal (0.66,0.25,0.71), area 4.8mm2, adj f0,f298,f299,f300,f301
  f304: plane 0.71x0.41mm, normal (0,0,-1), area 0mm2, adj f2,f305,f309
  f305: plane 1.41x0.81mm, normal (-0.5,0.87,0), area 0.7mm2, adj f304,f307,f308,f309
  f306: plane 0.96x0.55mm, normal (0.5,-0.87,0), area 0.3mm2, adj f0,f307,f309
  f307: plane 4.56x3.18mm, normal (-0.59,-0.39,0.71), area 4.8mm2, adj f0,f305,f306,f308,f309
  f308: plane 0.7x0.42mm, normal (0,0,-1), area 0mm2, adj f2,f305,f307
  f309: plane 4.69x2.95mm, normal (0.63,0.32,0.71), area 4.8mm2, adj f0,f304,f305,f306,f307
  f310: plane 0.67x0.48mm, normal (0,0,-1), area 0mm2, adj f2,f311,f315
  f311: plane 1.31x0.95mm, normal (-0.59,0.81,0), area 0.7mm2, adj f310,f313,f314,f315
  f312: plane 0.89x0.65mm, normal (0.59,-0.81,0), area 0.3mm2, adj f0,f313,f315
  f313: plane 4.33x3.56mm, normal (-0.55,-0.45,0.71), area 4.8mm2, adj f0,f311,f312,f314,f315
  f314: plane 0.66x0.49mm, normal (0,0,-1), area 0mm2, adj f2,f311,f313
  f315: plane 4.48x3.36mm, normal (0.59,0.39,0.71), area 4.8mm2, adj f0,f310,f311,f312,f313
  f316: plane 0.62x0.54mm, normal (0,0,-1), area 0mm2, adj f2,f317,f321
  f317: plane 1.21x1.09mm, normal (-0.67,0.74,0), area 0.7mm2, adj f316,f319,f320,f321
  f318: plane 0.82x0.74mm, normal (0.67,-0.74,0), area 0.3mm2, adj f0,f319,f321
  f319: plane 4.05x3.91mm, normal (-0.5,-0.5,0.71), area 4.8mm2, adj f0,f317,f318,f320,f321
  f320: plane 0.6x0.56mm, normal (0,0,-1), area 0mm2, adj f2,f317,f319
  f321: plane 4.22x3.72mm, normal (0.55,0.45,0.71), area 4.8mm2, adj f0,f316,f317,f318,f319
  f322: plane 0.6x0.56mm, normal (0,0,-1), area 0mm2, adj f2,f323,f327
  f323: plane 1.21x1.09mm, normal (-0.74,0.67,0), area 0.7mm2, adj f322,f325,f326,f327
  f324: plane 0.82x0.74mm, normal (0.74,-0.67,0), area 0.3mm2, adj f0,f325,f327
  f325: plane 4.22x3.72mm, normal (-0.45,-0.55,0.71), area 4.8mm2, adj f0,f323,f324,f326,f327
  f326: plane 0.62x0.54mm, normal (0,0,-1), area 0mm2, adj f2,f323,f325
  f327: plane 4.05x3.91mm, normal (0.5,0.5,0.71), area 4.8mm2, adj f0,f322,f323,f324,f325
  f328: plane 0.66x0.49mm, normal (0,0,-1), area 0mm2, adj f2,f329,f333
  f329: plane 1.31x0.95mm, normal (-0.81,0.59,0), area 0.7mm2, adj f328,f331,f332,f333
  f330: plane 0.89x0.65mm, normal (0.81,-0.59,0), area 0.3mm2, adj f0,f331,f333
  f331: plane 4.48x3.36mm, normal (-0.39,-0.59,0.71), area 4.8mm2, adj f0,f329,f330,f332,f333
  f332: plane 0.67x0.48mm, normal (0,0,-1), area 0mm2, adj f2,f329,f331
  f333: plane 4.33x3.56mm, normal (0.45,0.55,0.71), area 4.8mm2, adj f0,f328,f329,f330,f331
  f334: plane 0.7x0.42mm, normal (0,0,-1), area 0mm2, adj f2,f335,f339
  f335: plane 1.41x0.81mm, normal (-0.87,0.5,0), area 0.7mm2, adj f334,f337,f338,f339
  f336: plane 0.96x0.55mm, normal (0.87,-0.5,0), area 0.3mm2, adj f0,f337,f339
  f337: plane 4.69x2.95mm, normal (-0.32,-0.63,0.71), area 4.8mm2, adj f0,f335,f336,f338,f339
  f338: plane 0.71x0.41mm, normal (0,0,-1), area 0mm2, adj f2,f335,f337
  f339: plane 4.56x3.18mm, normal (0.39,0.59,0.71), area 4.8mm2, adj f0,f334,f335,f336,f337
  f340: plane 0.74x0.35mm, normal (0,0,-1), area 0mm2, adj f2,f341,f345
  f341: plane 1.48x0.81mm, normal (-0.91,0.41,0), area 0.7mm2, adj f340,f343,f344,f345
  f342: plane 1.01x0.55mm, normal (0.91,-0.41,0), area 0.3mm2, adj f0,f343,f345
  f343: plane 4.85x2.52mm, normal (-0.25,-0.66,0.71), area 4.8mm2, adj f0,f341,f342,f344,f345
  f344: plane 0.75x0.33mm, normal (0,0,-1), area 0mm2, adj f2,f341,f343
  f345: plane 4.74x2.75mm, normal (0.32,0.63,0.71), area 4.8mm2, adj f0,f340,f341,f342,f343
  f346: plane 0.77x0.27mm, normal (0,0,-1), area 0mm2, adj f2,f347,f351
  f347: plane 1.54x0.81mm, normal (-0.95,0.31,0), area 0.7mm2, adj f346,f349,f350,f351
  f348: plane 1.05x0.55mm, normal (0.95,-0.31,0), area 0.3mm2, adj f0,f349,f351
  f349: plane 4.96x2.05mm, normal (-0.18,-0.68,0.71), area 4.8mm2, adj f0,f347,f348,f350,f351
  f350: plane 0.78x0.25mm, normal (0,0,-1), area 0mm2, adj f2,f347,f349
  f351: plane 4.88x2.3mm, normal (0.25,0.66,0.71), area 4.8mm2, adj f0,f346,f347,f348,f349
  f352: plane 0.79x0.19mm, normal (0,0,-1), area 0mm2, adj f2,f353,f357
  f353: plane 1.59x0.81mm, normal (-0.98,0.21,0), area 0.7mm2, adj f352,f355,f356,f357
  f354: plane 1.08x0.55mm, normal (0.98,-0.21,0), area 0.3mm2, adj f0,f355,f357
  f355: plane 5.01x1.57mm, normal (-0.11,-0.7,0.71), area 4.8mm2, adj f0,f353,f354,f356,f357
  f356: plane 0.8x0.17mm, normal (0,0,-1), area 0mm2, adj f2,f353,f355
  f357: plane 4.95x1.82mm, normal (0.18,0.68,0.71), area 4.8mm2, adj f0,f352,f353,f354,f355
  f358: plane 0.81x0.11mm, normal (0,0,-1), area 0mm2, adj f2,f359,f363
  f359: plane 1.61x0.81mm, normal (-0.99,0.1,0), area 0.7mm2, adj f358,f361,f362,f363
  f360: plane 1.1x0.55mm, normal (0.99,-0.1,0), area 0.3mm2, adj f0,f361,f363
  f361: plane 5.01x1.07mm, normal (-0.04,-0.71,0.71), area 4.8mm2, adj f0,f359,f360,f362,f363
  f362: plane 0.81x0.08mm, normal (0,0,-1), area 0mm2, adj f2,f359,f361
  f363: plane 4.98x1.32mm, normal (0.11,0.7,0.71), area 4.8mm2, adj f0,f358,f359,f360,f361
PART B: 37 faces, bbox 40x3x60 mm
  f0: plane 30x3mm, normal (0,0,1), area 90mm2, adj f1,f7,f8,f9
  f1: cylinder r=5mm len=5mm, axis (0,1,0), area 23.6mm2, adj f0,f2,f8,f9
  f2: plane 50x3mm, normal (-1,0,0), area 150mm2, adj f1,f3,f8,f9
  f3: cylinder r=5mm len=5mm, axis (0,1,0), area 23.6mm2, adj f2,f4,f8,f9
  f4: plane 30x3mm, normal (0,0,-1), area 90mm2, adj f3,f5,f8,f9
  f5: cylinder r=5mm len=5mm, axis (0,1,0), area 23.6mm2, adj f4,f6,f8,f9
  f6: plane 50x3mm, normal (1,0,0), area 150mm2, adj f5,f7,f8,f9
  f7: cylinder r=5mm len=5mm, axis (0,1,0), area 23.6mm2, adj f0,f6,f8,f9
  f8: plane 60x40mm, normal (0,-1,0), area 2350.3mm2, adj f0,f1,f2,f3,f4,f5,f6,f7
  f9: plane 60x40mm, normal (0,1,0), area 2064.4mm2, adj f0,f1,f2,f3,f4,f5,f6,f7
  f10: cylinder r=10mm len=20mm, axis (0,1,0), area 125.7mm2, adj f9,f11
  f11: plane 20x20mm, normal (0,1,0), area 210.5mm2, adj f10,f12,f13,f14,f15,f16,f17,f18
  f12: sphere r=1.01mm, area 5.7mm2, adj f11
  f13: sphere r=1.01mm, area 5.7mm2, adj f11
  f14: sphere r=1.01mm, area 5.7mm2, adj f11
  f15: sphere r=1.01mm, area 5.7mm2, adj f11
  f16: sphere r=1.01mm, area 5.7mm2, adj f11
  f17: sphere r=1.01mm, area 5.7mm2, adj f11
  f18: sphere r=1.01mm, area 5.7mm2, adj f11
  f19: sphere r=1.01mm, area 5.7mm2, adj f11
  f20: sphere r=1.01mm, area 5.7mm2, adj f11
  f21: sphere r=1.01mm, area 5.7mm2, adj f11
  f22: sphere r=1.01mm, area 5.7mm2, adj f11
  f23: sphere r=1.01mm, area 5.7mm2, adj f11
  f24: sphere r=1.01mm, area 5.7mm2, adj f11
  f25: sphere r=1.01mm, area 5.7mm2, adj f11
  f26: sphere r=1.01mm, area 5.7mm2, adj f11
  f27: sphere r=1.01mm, area 5.7mm2, adj f11
  f28: sphere r=1.01mm, area 5.7mm2, adj f11
  f29: sphere r=1.01mm, area 5.7mm2, adj f11
  f30: sphere r=1.01mm, area 5.7mm2, adj f11
  f31: sphere r=1.01mm, area 5.7mm2, adj f11
  f32: sphere r=1.01mm, area 5.7mm2, adj f11
  f33: sphere r=1.01mm, area 5.7mm2, adj f11
  f34: sphere r=1.01mm, area 5.7mm2, adj f11
  f35: sphere r=1.01mm, area 5.7mm2, adj f11
  f36: cylinder r=3mm len=6mm, axis (0,1,0), area 18.8mm2, adj f8,f11
PLACE A rot(axis=(0.58,-0.58,0.58),120deg) t=(0,6,0)mm
PLACE B at identity
MATE fastened A.f2 <-> B.f36  axis (0,1,0) through (0,4,0)mm
